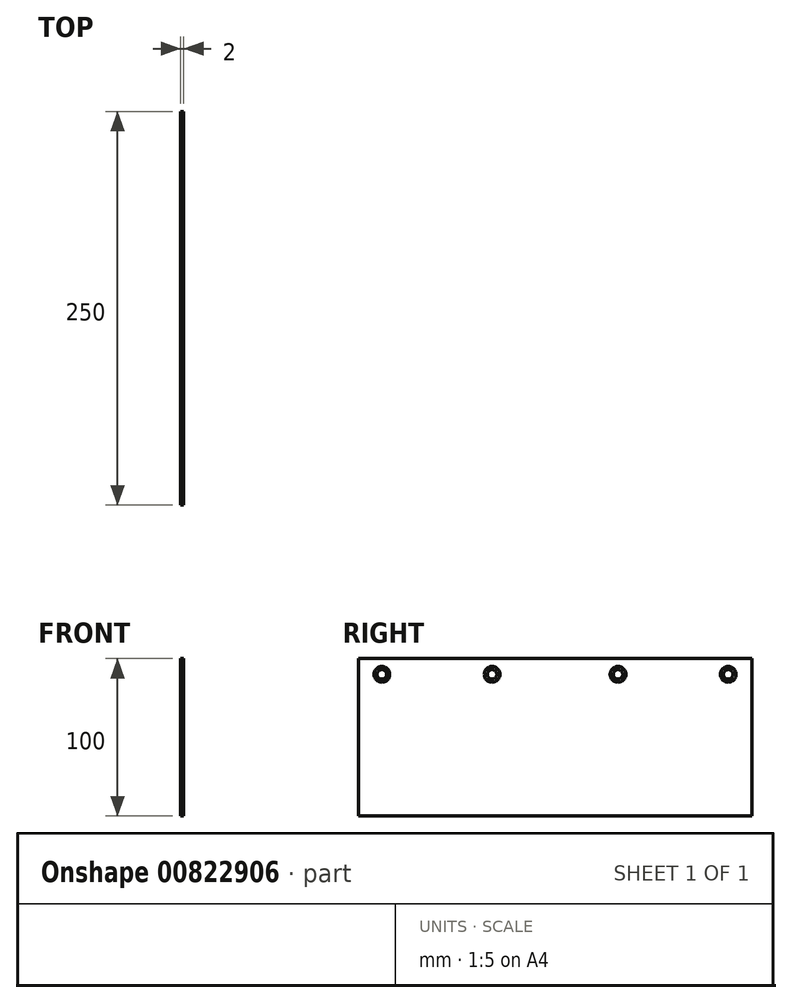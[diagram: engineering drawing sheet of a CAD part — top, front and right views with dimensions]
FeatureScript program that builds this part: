
annotation { "Feature Type Name" : "Feature", "Feature Type Description" : "" }
export const myFeature = defineFeature(function(context is Context, id is Id, definition is map)
    precondition{}
    {
        {
            var Q0;
            Q0=qCreatedBy(makeId("Right.planeOp"),FACE);
            var sketch = newSketch(context, id + "F0", { "sketchPlane" : qUnion([Q0])});
            skLineSegment(sketch, "E0.bottom", {"start": v(-125, -50) * mm, "end": v(125, -50) * mm});
            skLineSegment(sketch, "E0.top", {"start": v(-125, 50) * mm, "end": v(125, 50) * mm});
            skLineSegment(sketch, "E0.left", {"start": v(-125, -50) * mm, "end": v(-125, 50) * mm});
            skLineSegment(sketch, "E0.right", {"start": v(125, -50) * mm, "end": v(125, 50) * mm});
            skPoint(sketch, "E0.middle", {"position": v(0, 0) * mm});
            skLineSegment(sketch, "E1", {"start": v(0, 0) * mm, "end": v(0, 40) * mm, "construction": true});
            skLineSegment(sketch, "E2", {"start": v(0, 40) * mm, "end": v(-40, 40) * mm, "construction": true});
            skLineSegment(sketch, "E3", {"start": v(-40, 40) * mm, "end": v(-110, 40) * mm, "construction": true});
            skCircle(sketch, "E4", {"center": v(-110, 40) * mm, "radius": 3 * mm});
            skCircle(sketch, "E5", {"center": v(-40, 40) * mm, "radius": 3 * mm});
            skCircle(sketch, "E6.MirrorC", {"center": v(40, 40) * mm, "radius": 3 * mm});
            skCircle(sketch, "E7.MirrorC", {"center": v(110, 40) * mm, "radius": 3 * mm});
            skSolve(sketch);
        }
        {
            var Q0;
            Q0 = qSketchRegion(id + "F0", true);
            extrude(context, id + "F1", {"entities" : qUnion([Q0]), "depth" : 2 * mm, "offsetDistance" : 25 * mm});
        }
        {
            var Q0;
            Q0=makeQuery(id+"F1.opExtrude","CAP_EDGE",EDGE,{"disambiguationData":[OSD([sQuery(id+"F0.wireOp",EDGE,"E4")])],"isStart":false});
            var Q1;
            Q1=makeQuery(id+"F1.opExtrude","CAP_EDGE",EDGE,{"disambiguationData":[OSD([sQuery(id+"F0.wireOp",EDGE,"E5")])],"isStart":false});
            var Q2;
            Q2=makeQuery(id+"F1.opExtrude","CAP_EDGE",EDGE,{"disambiguationData":[OSD([sQuery(id+"F0.wireOp",EDGE,"E6.MirrorC")])],"isStart":false});
            var Q3;
            Q3=makeQuery(id+"F1.opExtrude","CAP_EDGE",EDGE,{"disambiguationData":[OSD([sQuery(id+"F0.wireOp",EDGE,"E7.MirrorC")])],"isStart":false});
            chamfer(context, id + "F2", {"entities" : qUnion([Q0, Q1, Q2, Q3]), "width" : 2 * mm, "tangentPropagation" : true});
        }
    });
